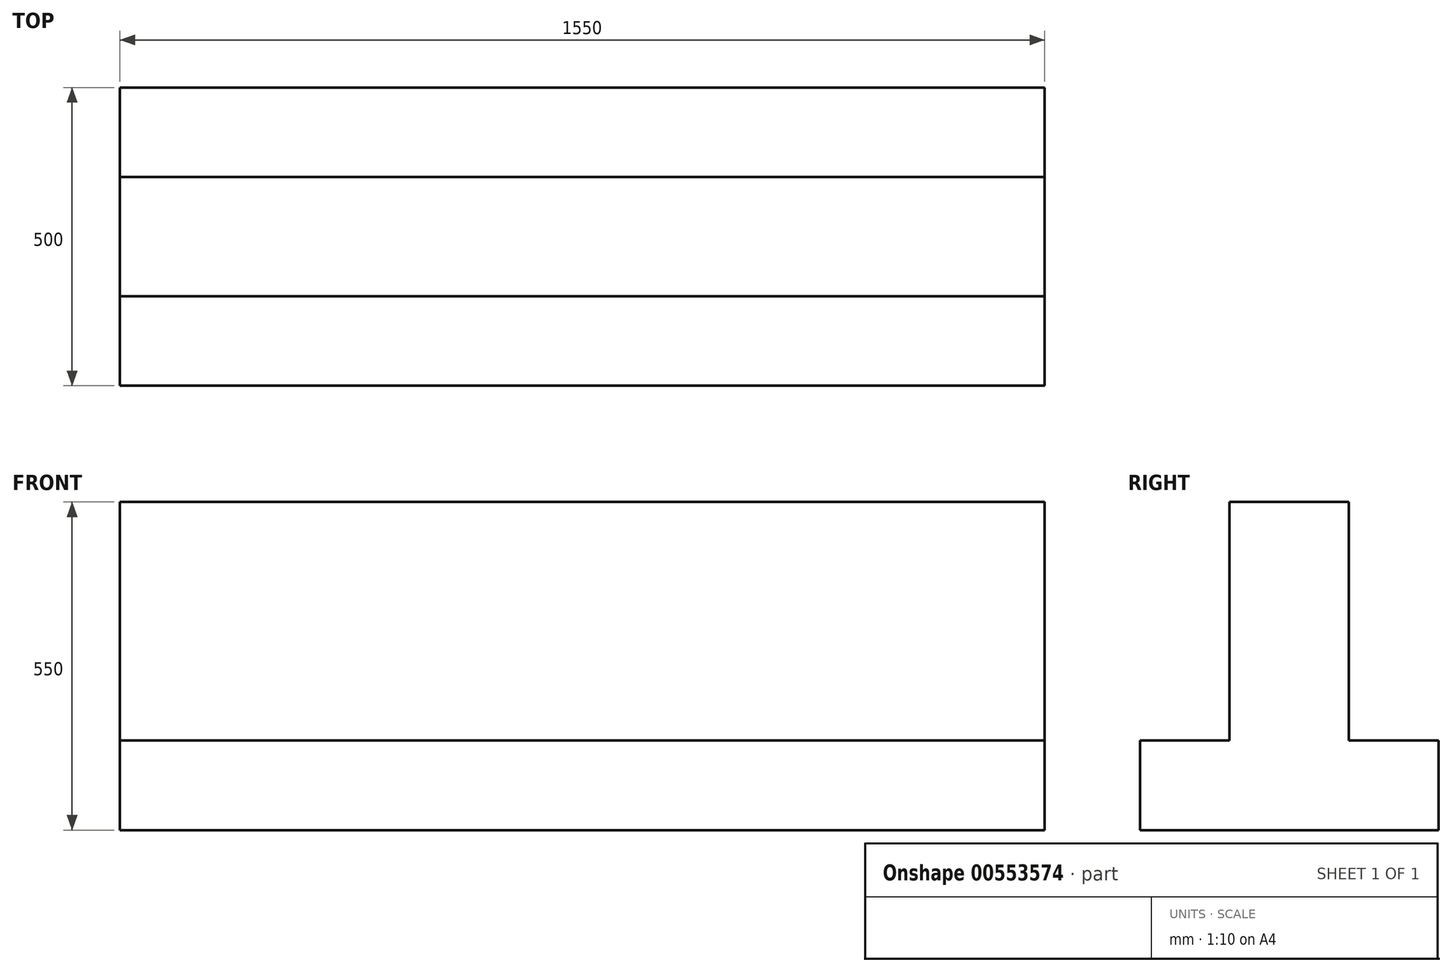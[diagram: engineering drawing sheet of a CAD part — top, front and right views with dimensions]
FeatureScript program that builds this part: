
annotation { "Feature Type Name" : "Feature", "Feature Type Description" : "" }
export const myFeature = defineFeature(function(context is Context, id is Id, definition is map)
    precondition{}
    {
        {
            var Q0;
            Q0=qCreatedBy(makeId("Right.planeOp"),FACE);
            var sketch = newSketch(context, id + "F0", { "sketchPlane" : qUnion([Q0])});
            skLineSegment(sketch, "E0", {"start": v(-150, -449.86) * mm, "end": v(350, -449.86) * mm});
            skLineSegment(sketch, "E1", {"start": v(350, -449.86) * mm, "end": v(350, -299.86) * mm});
            skLineSegment(sketch, "E2", {"start": v(350, -299.86) * mm, "end": v(200, -299.86) * mm});
            skLineSegment(sketch, "E3", {"start": v(200, -299.86) * mm, "end": v(200, 100.14) * mm});
            skLineSegment(sketch, "E4", {"start": v(200, 100.14) * mm, "end": v(0, 100.14) * mm});
            skLineSegment(sketch, "E5", {"start": v(0, 100.14) * mm, "end": v(0, -299.86) * mm});
            skLineSegment(sketch, "E6", {"start": v(0, -299.86) * mm, "end": v(-150, -299.86) * mm});
            skLineSegment(sketch, "E7", {"start": v(-150, -299.86) * mm, "end": v(-150, -449.86) * mm});
            skSolve(sketch);
        }
        {
            var Q0;
            Q0 = qSketchRegion(id + "F0", true);
            extrude(context, id + "F1", {"entities" : qUnion([Q0]), "oppositeDirection" : true, "depth" : 1550 * mm, "offsetDistance" : 25 * mm});
        }
    });
